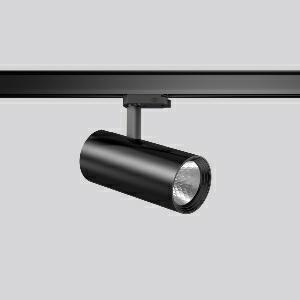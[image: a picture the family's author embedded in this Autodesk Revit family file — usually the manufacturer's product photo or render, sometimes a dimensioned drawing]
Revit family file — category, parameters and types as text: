
# Revit family: deecos_s_mini_742204_003_1b1f
name_source: partatom
category: Lighting Fixtures
units: mm (PartAtom-declared; Revit-internal decimal feet)

## family parameters
Cut with Voids When Loaded = No
Host = Face
Light Source = No
Part Type = Normal
Room Calculation Point = No
Round Connector Dimension = Use Diameter
Shared = No

## types (1)
- DEECOS S mini (1 x LED Modul 930, 3500 lm, 3000)
    Apparent Load = 29 VA
    Approval mark = CE
    CIE Flux Codes = 99 100 100 100 100
    Color Rendering = 90
    Color Temperature = 3000
    Default Elevation = 1800 mm
    Description = Series: DEECOS S mini
LED surface-mounted projector in modern design with no visible cooling ribs. Housing: die-cast aluminium, powder-coated. Rotation range: 356°. Swivel range: 90°. Black plastic ring and recessed LED to prevent glare from the side. Optical assembly with reflector made of MIRO-Silver with 98% total light reflection for outstanding efficiency - can be changed without tools. Best colour rendering index Ra>90. With multi adaptor for 3-circuit tracks 230 V. Suitable for Track on ceiling, Wall track. High quality converter without flickering and stroboscopic effect. The following accessories can be mounted without use of tools: interchangeable lenses, decorative glasses, honeycomb louvre, clear and frosted diffusers, white interchangeable plastic ring. 
Colour: deep black, matt (RAL 9005)
Diameter: 87 mm
Height: 214 mm
Lamp: LED
Socket: without socket
Colour temperature: 3000K
Colour rendering index (CRI): 92
System power: 29 W
Rated luminous flux: 3500 lm
Luminous efficiency: 121 lm/W
Control gear: Regulated power supply
Protection class: I
Type of protection: IP 20
    Height = 214 mm
    Lamp = 1 x LED Modul 930
    Lamp Light Flux = 3500 lm
    Lamp count = 1
    Length = 87 mm
    Lifetime = 50000 h
    Luminous efficacy = 121 lm/W
    Manufacturer = RZB
    ModVariant = No
    Model = 742204.003
    Mounting Place = Ceiling
    Mounting Type = Rail mounted
    Number of Poles = 1
    OnlyDefault = Yes
    Power Factor = 1
    Product Name = DEECOS S mini
    Product group = Track mounted projectors
    ProductGroupID = 301
    Protection Class = Protection class I
    Protection Degree = IP 20
    RLX_Detail_Level = 1
    RLX_Emergency_Light_Flux = 0 lm
    RLX_Emergency_Type = 0
    RLX_Emergency_Type_DB = No
    RlxData = <blob elided: 38445 chars, md5=b3491097>
    Socket = socket
    Standby Power = 0 W
    System Light Flux = 3500 lm
    System Power = 29 W
    Type Comments = Product without accessories
    Type Image = 741926.003.jpg
    URL = http://relux.com
    VarID = ---
    Voltage = 230 V
    Voltage Range = 220-240 V
    Weight = 0.00 kg
    Width = 0 mm  [stored 0 ft]

note: [stored X ft] marks values corroborated as IEEE doubles in the binary element streams (Revit-internal decimal feet)

## geometry (parser evidence)
native form markers: Blend x4, Sweep x13
no freeform markers — native parametric forms only
